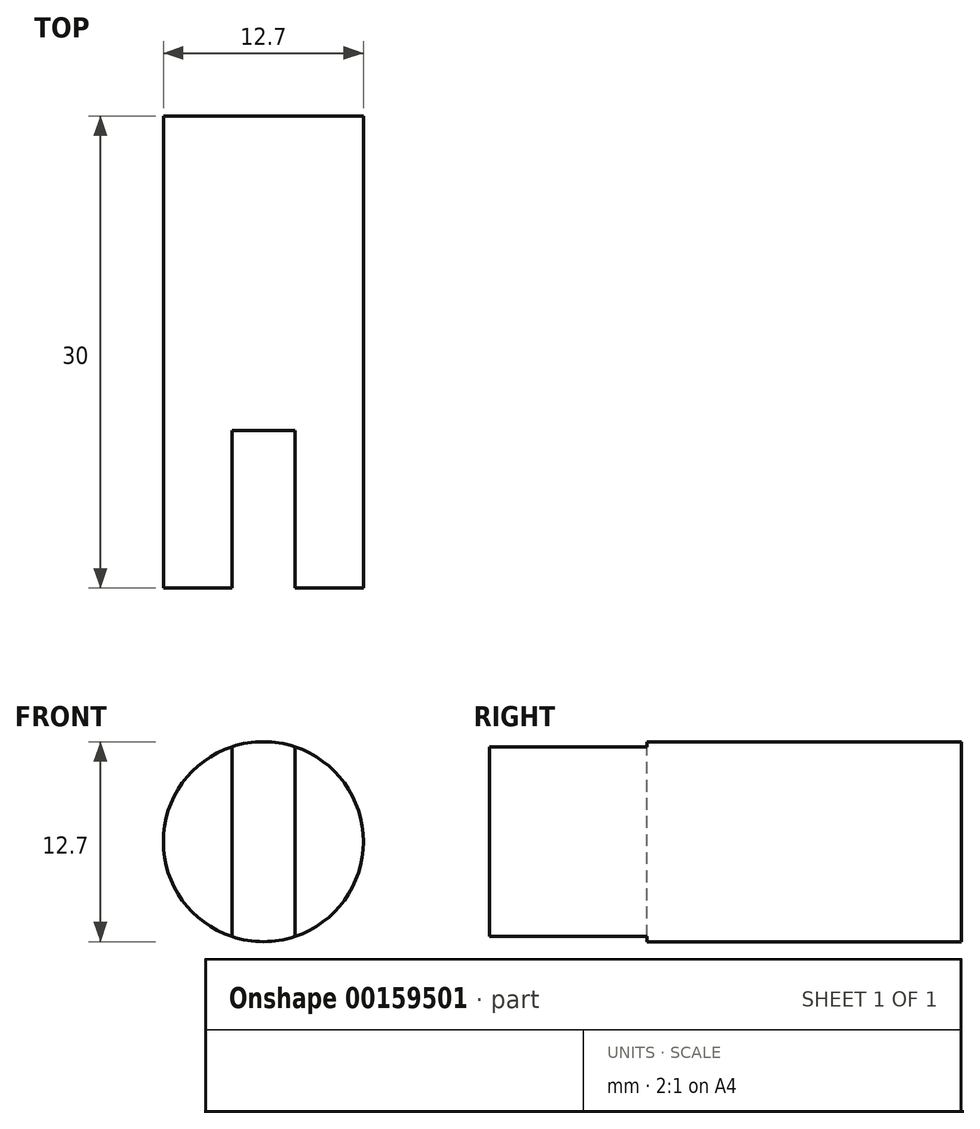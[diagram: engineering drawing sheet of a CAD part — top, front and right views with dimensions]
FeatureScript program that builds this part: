
annotation { "Feature Type Name" : "Feature", "Feature Type Description" : "" }
export const myFeature = defineFeature(function(context is Context, id is Id, definition is map)
    precondition{}
    {
        {
            var Q0;
            Q0=qCreatedBy(makeId("Front.planeOp"),FACE);
            var sketch = newSketch(context, id + "F0", { "sketchPlane" : qUnion([Q0])});
            skCircle(sketch, "E0", {"center": v(0, 0) * mm, "radius": 6.35 * mm});
            skSolve(sketch);
        }
        {
            var Q0;
            Q0 = qSketchRegion(id + "F0", true);
            extrude(context, id + "F1", {"entities" : qUnion([Q0]), "depth" : 30 * mm});
        }
        {
            var Q0;
            Q0=makeQuery(id+"F1.opExtrude","CAP_FACE",FACE,{"disambiguationData":[OSD([sQuery(id+"F0.wireOp",EDGE,"E0")])],"isStart":false});
            var sketch = newSketch(context, id + "F2", { "sketchPlane" : qUnion([Q0])});
            skLineSegment(sketch, "E1.bottom", {"start": v(-2, -8.05) * mm, "end": v(2, -8.05) * mm});
            skLineSegment(sketch, "E1.top", {"start": v(-2, 8.05) * mm, "end": v(2, 8.05) * mm});
            skLineSegment(sketch, "E1.left", {"start": v(-2, -8.05) * mm, "end": v(-2, 8.05) * mm});
            skLineSegment(sketch, "E1.right", {"start": v(2, -8.05) * mm, "end": v(2, 8.05) * mm});
            skPoint(sketch, "E1.middle", {"position": v(0, 0) * mm});
            skSolve(sketch);
        }
        {
            var Q0;
            Q0 = qSketchRegion(id + "F2", true);
            extrude(context, id + "F3", {"entities" : qUnion([Q0]), "operationType" : NewBodyOperationType.REMOVE, "oppositeDirection" : true, "depth" : 10 * mm});
        }
    });
